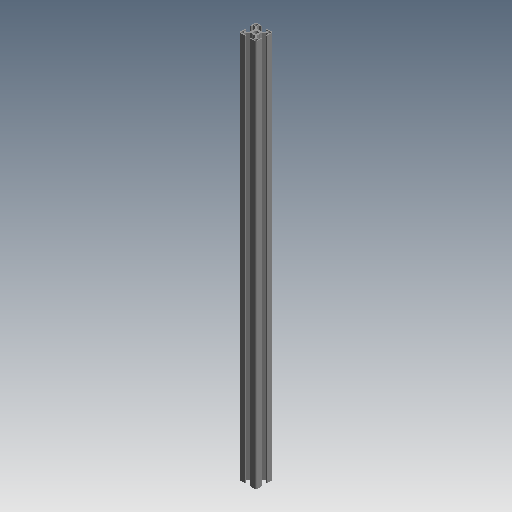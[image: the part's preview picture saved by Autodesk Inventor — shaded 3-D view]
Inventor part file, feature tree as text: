
AUTODESK INVENTOR PART (.ipt)
format: ipt  version: 2020 (Build 240168000, 168)  size: 211,968 bytes
history: native  units: mm (DEFAULTED — no unit token found)
features: other x21, sketch x3, hole x2, extrude x1, pattern_linear x1
ambient origin geometry x8: Origin, YZ Plane, XZ Plane, XY Plane, X Axis, Y Axis, Z Axis, Center Point
bodies: Solid1 (feature_tree)
feature tree (28):
  extrude  "Extrusion1"  Depth=690.0mm
  hole  "Hole1"  [1 undecoded]
  hole  "Hole2"  [1 undecoded]
  pattern_linear  "Rectangular Pattern1"  [2 undecoded]
  other  "C1_XY"
  other  "C1_YZ"
  other  "C1_ZX"
  other  "C1_X"
  other  "C1_Y"
  other  "C1_Z"
  other  "C1_Center"
  other  "to_frame_cap1_XY"
  other  "to_frame_cap1_YZ"
  other  "to_frame_cap1_ZX"
  other  "to_frame_cap1_X"
  other  "to_frame_cap1_Y"
  other  "to_frame_cap1_Z"
  other  "to_frame_cap1_Center"
  other  "to_frame_cap2_XY"
  other  "to_frame_cap2_YZ"
  other  "to_frame_cap2_ZX"
  other  "to_frame_cap2_X"
  other  "to_frame_cap2_Y"
  other  "to_frame_cap2_Z"
  other  "to_frame_cap2_Center"
  sketch  "Sketch_1"  dims[d0=690.0mm d1=0.0mm]
  sketch  "Sketch2"  dims[d2=6.8mm d3=6.0mm d4=4.0mm d5=2.0mm d6=90.0deg d7=690.0mm d8=0.0mm]
  sketch  "Sketch3"  dims[d9=4.2mm d10=6.0mm d11=4.0mm d12=2.0mm d13=90.0deg d14=690.0mm d15=0.0mm d16=20.0mm d18=23.2mm d19=20.0mm d21=23.2mm d22=0.0mm d23=0.0mm d24=0.0mm]
note: 4 required parameter values undecoded (feature->parameter linkage not recoverable at this tier; creation-order binding heuristic only, values carry confidence <= 0.55)
